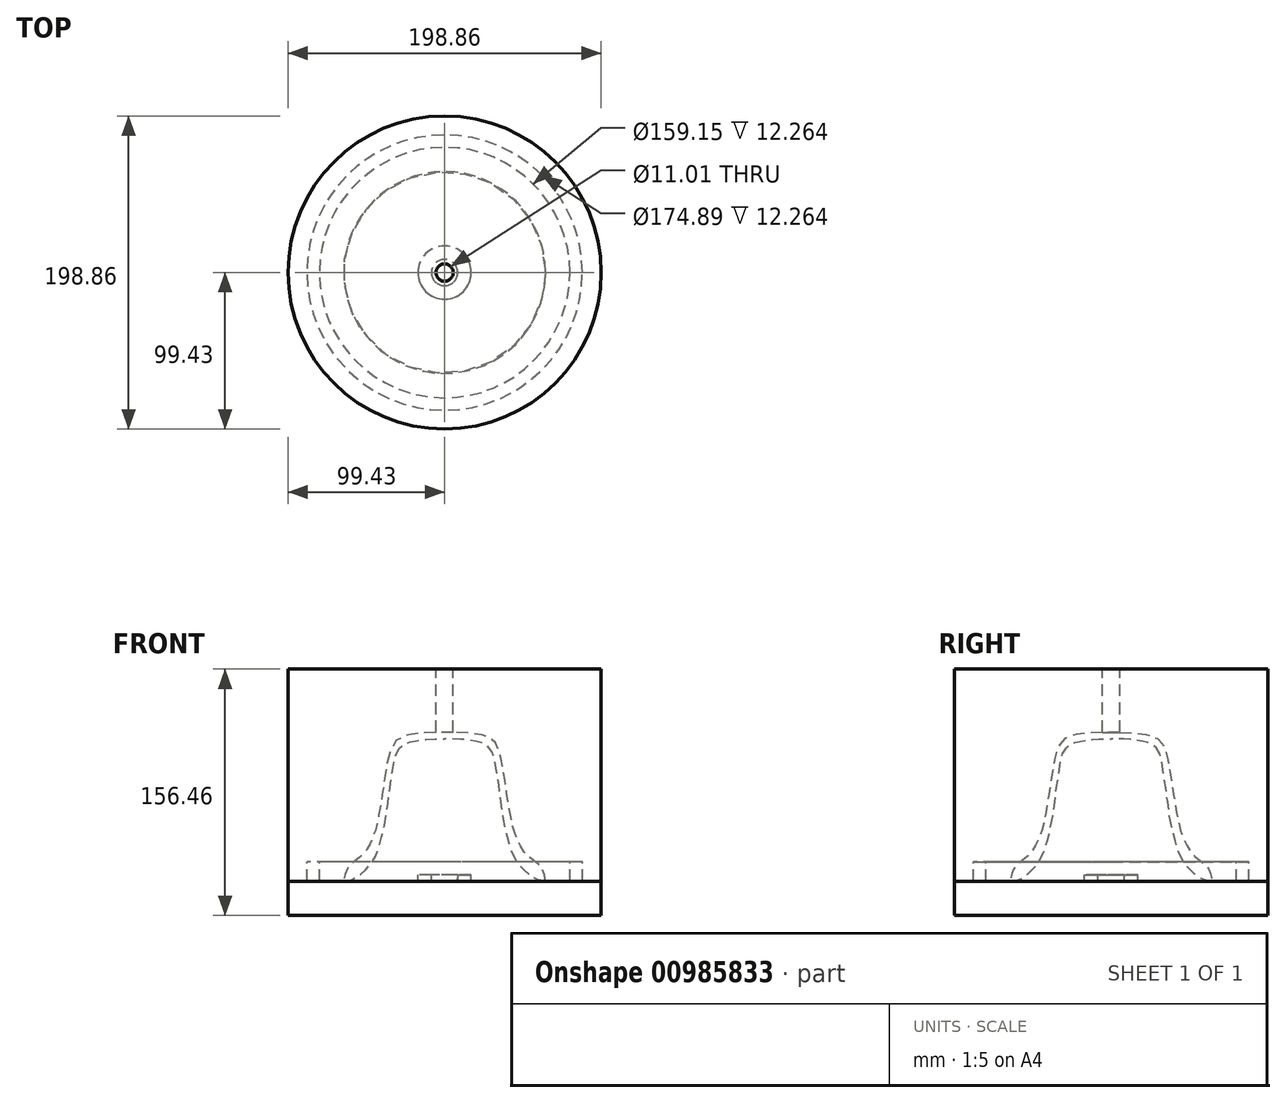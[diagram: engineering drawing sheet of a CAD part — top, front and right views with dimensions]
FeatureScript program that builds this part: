
annotation { "Feature Type Name" : "Feature", "Feature Type Description" : "" }
export const myFeature = defineFeature(function(context is Context, id is Id, definition is map)
    precondition{}
    {
        {
            var Q0;
            Q0=qCreatedBy(makeId("Front.planeOp"),FACE);
            var sketch = newSketch(context, id + "F0", { "sketchPlane" : qUnion([Q0])});
            skLineSegment(sketch, "E0", {"start": v(0, 149.58) * mm, "end": v(0, -169.13) * mm, "construction": true});
            skLineSegment(sketch, "E1", {"start": v(-5.5, 83.35) * mm, "end": v(-5.5, 43.2) * mm});
            skLineSegment(sketch, "E2", {"start": v(-5.5, 83.35) * mm, "end": v(-99.43, 83.35) * mm});
            skLineSegment(sketch, "E3", {"start": v(-99.43, 83.35) * mm, "end": v(-99.43, -51.37) * mm});
            skLineSegment(sketch, "E4", {"start": v(-99.43, -51.37) * mm, "end": v(-87.45, -51.37) * mm});
            skLineSegment(sketch, "E5", {"start": v(-87.45, -51.37) * mm, "end": v(-87.45, -39.1) * mm});
            skLineSegment(sketch, "E6", {"start": v(-87.45, -39.1) * mm, "end": v(-79.57, -39.1) * mm});
            skLineSegment(sketch, "E7", {"start": v(-79.57, -39.1) * mm, "end": v(-79.57, -51.37) * mm});
            skLineSegment(sketch, "E8", {"start": v(-79.57, -51.37) * mm, "end": v(-64, -51.37) * mm});
            skFitSpline(sketch, "E9", {"points": [v(-64, -51.37) * mm, v(-62.46, -44.53) * mm, v(-59.59, -40.65) * mm, v(-54.73, -36.8) * mm, v(-50.14, -32.38) * mm, v(-46.92, -26.33) * mm, v(-43.97, -18.96) * mm, v(-41.8, -9.03) * mm, v(-40.18, 0) * mm, v(-37.01, 20.44) * mm, v(-33.76, 33.53) * mm, v(-28.9, 39.6) * mm, v(-5.5, 43.2) * mm], "startDerivative": vector(-4.01, 64.87) * mm, "endDerivative": vector(280.27, 9.12) * mm});
            skSolve(sketch);
        }
        {
            var Q0;
            Q0 = qSketchRegion(id + "F0", true);
            var Q1;
            Q1=sQuery(id+"F0.wireOp",EDGE,"E0");
            revolve(context, id + "F1", {"surfaceOperationType" : NewSurfaceOperationType.NEW, "entities" : qUnion([Q0]), "axis" : qUnion([Q1]), "revolveType" : RevolveType.FULL});
        }
        {
            var Q0;
            Q0=qCreatedBy(makeId("Front.planeOp"),FACE);
            var sketch = newSketch(context, id + "F2", { "sketchPlane" : qUnion([Q0])});
            skLineSegment(sketch, "E10", {"start": v(0, 58.33) * mm, "end": v(0, -64.77) * mm, "construction": true});
            skPoint(sketch, "E11", {"position": v(-64, -51.37) * mm});
            skFitSpline(sketch, "E12", {"points": [v(-64, -51.37) * mm, v(-58.38, -50.26) * mm, v(-54.87, -48.06) * mm, v(-51.06, -44.85) * mm, v(-45.68, -38.68) * mm, v(-41.45, -28.69) * mm, v(-37.38, -11.73) * mm, v(-35.25, 4.24) * mm, v(-32.6, 21.61) * mm, v(-31.1, 28.8) * mm, v(-28.56, 33.39) * mm, v(-26.19, 35.42) * mm, v(-19.74, 37.63) * mm, v(-10.92, 38.82) * mm, v(0, 39.16) * mm], "startDerivative": vector(95.57, 12.91) * mm, "endDerivative": vector(137.77, 2.12) * mm});
            skLineSegment(sketch, "E13", {"start": v(-64, -51.37) * mm, "end": v(-16.92, -51.12) * mm});
            skLineSegment(sketch, "E14", {"start": v(-16.92, -51.12) * mm, "end": v(-16.95, -47.3) * mm});
            skLineSegment(sketch, "E15", {"start": v(-16.95, -47.3) * mm, "end": v(-8.38, -47.25) * mm});
            skLineSegment(sketch, "E16", {"start": v(-8.38, -47.25) * mm, "end": v(-8.36, -51.12) * mm});
            skLineSegment(sketch, "E17", {"start": v(-8.36, -51.12) * mm, "end": v(0, -51.07) * mm});
            skLineSegment(sketch, "E18", {"start": v(0, -51.07) * mm, "end": v(0, 39.16) * mm});
            skSolve(sketch);
        }
        {
            var Q0;
            Q0 = qSketchRegion(id + "F2", true);
            var Q1;
            Q1=sQuery(id+"F2.wireOp",EDGE,"E18");
            revolve(context, id + "F3", {"surfaceOperationType" : NewSurfaceOperationType.NEW, "entities" : qUnion([Q0]), "axis" : qUnion([Q1]), "revolveType" : RevolveType.FULL});
        }
        {
            var Q0;
            Q0=qCreatedBy(makeId("Front.planeOp"),FACE);
            var sketch = newSketch(context, id + "F4", { "sketchPlane" : qUnion([Q0])});
            skLineSegment(sketch, "E19.0", {"start": v(-99.43, -51.37) * mm, "end": v(-87.45, -51.37) * mm});
            skLineSegment(sketch, "E20.0", {"start": v(-87.45, -51.37) * mm, "end": v(-87.45, -39.1) * mm});
            skLineSegment(sketch, "E21.0", {"start": v(-87.45, -39.1) * mm, "end": v(-79.57, -39.1) * mm});
            skLineSegment(sketch, "E22.0", {"start": v(-79.57, -39.1) * mm, "end": v(-79.57, -51.37) * mm});
            skLineSegment(sketch, "E23.0", {"start": v(-79.57, -51.37) * mm, "end": v(-64, -51.37) * mm});
            skLineSegment(sketch, "E24.0", {"start": v(-64, -51.37) * mm, "end": v(-16.92, -51.12) * mm});
            skPoint(sketch, "E25.0", {"position": v(-16.94, -49.2) * mm});
            skLineSegment(sketch, "E26.0", {"start": v(-16.92, -51.12) * mm, "end": v(-16.95, -47.3) * mm});
            skLineSegment(sketch, "E27.0", {"start": v(-16.95, -47.3) * mm, "end": v(-8.38, -47.25) * mm});
            skLineSegment(sketch, "E28.0", {"start": v(-8.38, -47.25) * mm, "end": v(-8.36, -51.12) * mm});
            skLineSegment(sketch, "E29.0", {"start": v(-8.36, -51.12) * mm, "end": v(0, -51.07) * mm});
            skLineSegment(sketch, "E30", {"start": v(-99.43, -51.37) * mm, "end": v(-99.43, -73.1) * mm});
            skLineSegment(sketch, "E31", {"start": v(-99.43, -73.1) * mm, "end": v(0, -73.1) * mm});
            skLineSegment(sketch, "E32", {"start": v(0, -73.1) * mm, "end": v(0, -51.07) * mm});
            skLineSegment(sketch, "E33", {"start": v(0, -29.42) * mm, "end": v(0, -211.16) * mm, "construction": true});
            skSolve(sketch);
        }
        {
            var Q0;
            Q0=makeQuery(id+"F4.imprint","IMPRINT",FACE,{"disambiguationData":[TD([[makeQuery(id+"F4.imprint","IMPRINT",EDGE,{"derivedFrom":sQuery(id+"F4.wireOp",EDGE,"E19.0")}),-1.0]])]});
            var Q1;
            Q1=sQuery(id+"F4.wireOp",EDGE,"E33");
            revolve(context, id + "F5", {"surfaceOperationType" : NewSurfaceOperationType.NEW, "entities" : qUnion([Q0]), "axis" : qUnion([Q1]), "revolveType" : RevolveType.FULL});
        }
    });
